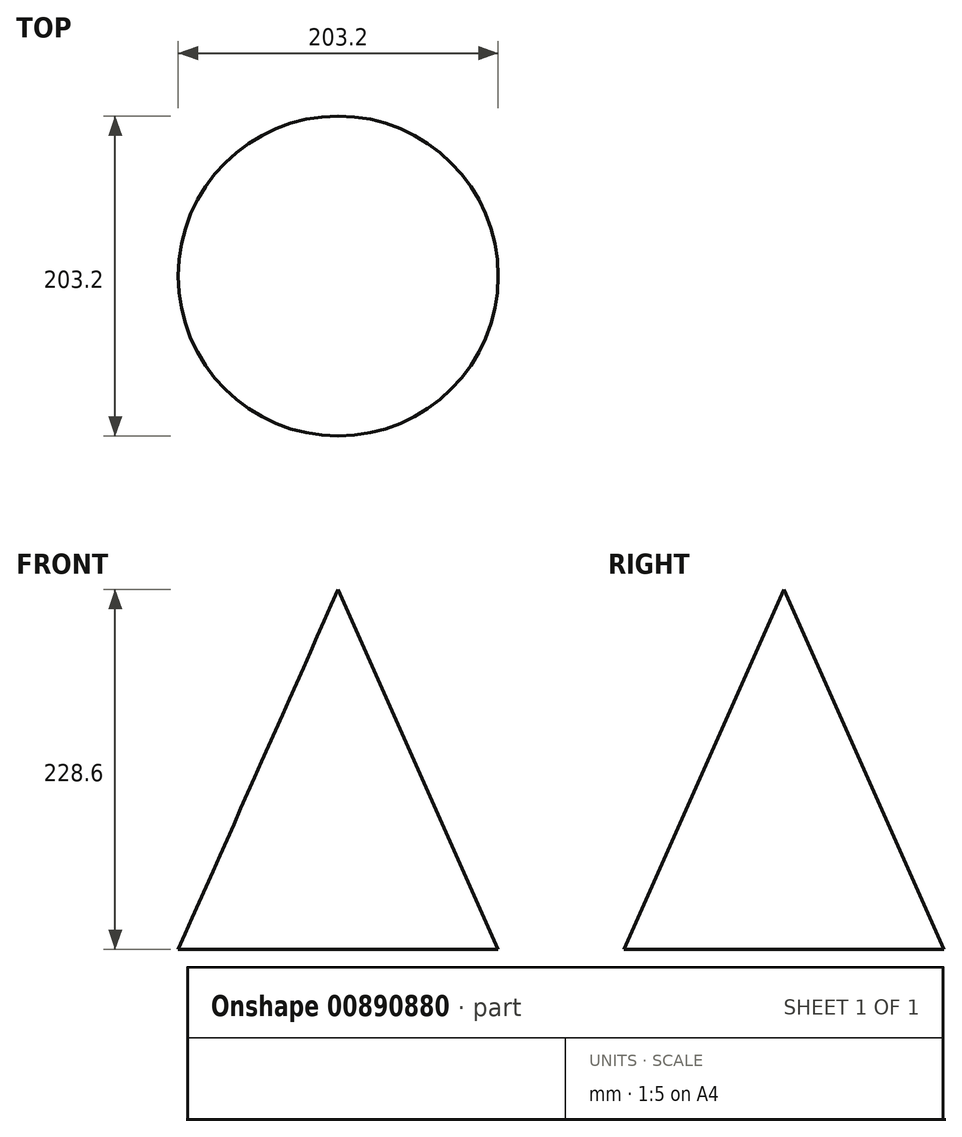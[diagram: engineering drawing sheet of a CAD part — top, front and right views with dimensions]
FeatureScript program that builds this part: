
annotation { "Feature Type Name" : "Feature", "Feature Type Description" : "" }
export const myFeature = defineFeature(function(context is Context, id is Id, definition is map)
    precondition{}
    {
        {
            var Q0;
            Q0=qCreatedBy(makeId("Front.planeOp"),FACE);
            var sketch = newSketch(context, id + "F0", { "sketchPlane" : qUnion([Q0])});
            skLineSegment(sketch, "E0", {"start": v(0, 228.6) * mm, "end": v(101.6, 0) * mm});
            skLineSegment(sketch, "E1", {"start": v(101.6, 0) * mm, "end": v(0, 0) * mm});
            skLineSegment(sketch, "E2", {"start": v(0, 0) * mm, "end": v(0, 228.6) * mm});
            skSolve(sketch);
        }
        {
            var Q0;
            Q0=makeQuery(id+"F0.imprint","IMPRINT",FACE,{"disambiguationData":[TD([[makeQuery(id+"F0.imprint","IMPRINT",EDGE,{"derivedFrom":sQuery(id+"F0.wireOp",EDGE,"E0")}),-1.0]])]});
            var Q1;
            Q1=sQuery(id+"F0.wireOp",EDGE,"E2");
            revolve(context, id + "F1", {"surfaceOperationType" : NewSurfaceOperationType.NEW, "entities" : qUnion([Q0]), "axis" : qUnion([Q1]), "revolveType" : RevolveType.FULL});
        }
    });
